# Revit family: ElectricalEquipment_Hager_Design30_Garage_2Way
name_source: partatom
category: Electrical Equipment
revit_build: Autodesk Revit 2015 (Build: 20160512_1515(x64)
units: mm (PartAtom-declared; Revit-internal decimal feet)

## types (2) — shared parameters
Assembly Code = D5010
AssetType = Fixed
BIMObjectName = Hager_ElectricalEquipment_DINRailEnclosure_VM004K
Category = ElectricalEquipment
ClassificationName = Uniclass2015
ClassificationValue = Pr_80_77_28_16
Colour = RAL9010WhiteGloss
Default Elevation = 500 mm  [stored 1.64042 ft]
DocumentationLiterature = http://www.hager.co.uk
DocumentationTechnical = http://www.hager.co.uk
DurationUnit = Years
ExpectedLife = 10
IfcExportAs = ElectricalEquipment
IfcExportType = ElectricalEquipment
Keynote = V
Mains Type = AC
Manufacturer = Hager
ManufacturerName = Hager
Material = MildSteel,ABS,AcousticComposite
NBSDescription = ElectricalEquipment
NBSObjectName = Hager_DINRailEnclosure_VM004K
NBSReference = Pr_80_77_28_16
Neutral Rating = 100.00%
NominalHeight = 103 mm
NominalLength = 240 mm
NominalWidth = 149 mm  [stored 0.488845 ft]
Shape = Rectangular
TypeName = ElectricalEquipment_DINRailEnclosure_VM004K
URL = http://www.hager.co.uk
Voltage = 230V
WarrantyDescription = See Manufacturer
WarrantyDurationParts = 2
WarrantyDurationUnit = Years
WarrantyGuarantorParts = 2
_BimstoreBibleVersion = V15
_DistributedBy = www.bimstore.co.uk
zero-valued in all types: NominalDepth, ReplacementCost, ServiceLifeDuration, WarrantyDurationLabor, _BimSpecGuid, _CurrentRevision

## per-type parameters (varying)
| type | Description | EAN | Features |
| VM24H | 2Way_MetalGarage_CU_40A_RCCB | 3250610841815 | 2Way_MetalGarage_CU_40A_RCCB |
| VM24HK | 2Way_MetalGarage_CU_40A_RCCB_KO | 3250610841822 | 2Way_MetalGarage_CU_40A_RCCB_KO |

note: column(s) folded — value = type name in every type: Model, ModelNumber, ModelReference, Type Comments

note: [stored X ft] marks values corroborated as IEEE doubles in the binary element streams (Revit-internal decimal feet)

## geometry (parser evidence)
native form markers: Blend x2, Sweep x5
no freeform markers — native parametric forms only
